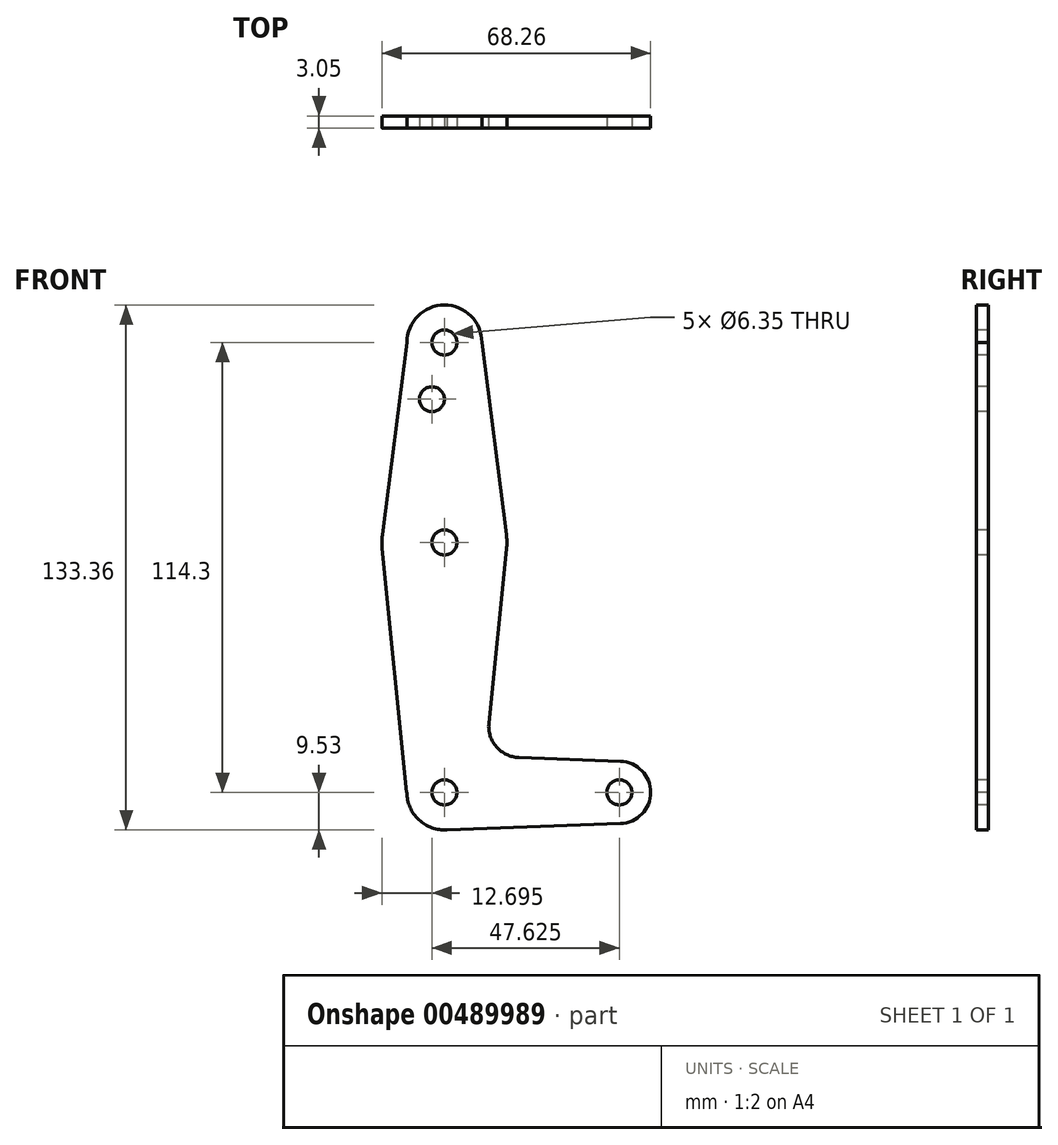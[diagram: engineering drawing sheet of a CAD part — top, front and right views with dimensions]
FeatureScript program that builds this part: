
annotation { "Feature Type Name" : "Feature", "Feature Type Description" : "" }
export const myFeature = defineFeature(function(context is Context, id is Id, definition is map)
    precondition{}
    {
        {
            var Q0;
            Q0=qCreatedBy(makeId("Front.planeOp"),FACE);
            var sketch = newSketch(context, id + "F0", { "sketchPlane" : qUnion([Q0])});
            skLineSegment(sketch, "E0", {"start": v(0, 114.3) * mm, "end": v(0, 0) * mm, "construction": true});
            skLineSegment(sketch, "E1", {"start": v(0, 0) * mm, "end": v(44.45, 0) * mm, "construction": true});
            skCircle(sketch, "E2", {"center": v(0, 114.3) * mm, "radius": 9.53 * mm});
            skCircle(sketch, "E3", {"center": v(0, 0) * mm, "radius": 9.53 * mm});
            skCircle(sketch, "E4", {"center": v(44.45, 0) * mm, "radius": 7.94 * mm});
            skCircle(sketch, "E5", {"center": v(0, 63.5) * mm, "radius": 15.88 * mm});
            skLineSegment(sketch, "E6", {"start": v(-9.57, 0) * mm, "end": v(9.53, 0) * mm});
            skLineSegment(sketch, "E7", {"start": v(0, 114.3) * mm, "end": v(9.52, 114.3) * mm});
            skLineSegment(sketch, "E8", {"start": v(9.53, 114.3) * mm, "end": v(15.75, 65.5) * mm});
            skLineSegment(sketch, "E9", {"start": v(-9.53, 114.3) * mm, "end": v(-15.75, 65.5) * mm});
            skLineSegment(sketch, "E10", {"start": v(-15.8, 61.91) * mm, "end": v(-9.57, 0) * mm});
            skLineSegment(sketch, "E11", {"start": v(15.8, 61.9) * mm, "end": v(11.3, 17.6) * mm});
            skLineSegment(sketch, "E12", {"start": v(18.93, 8.85) * mm, "end": v(44.73, 7.93) * mm});
            skLineSegment(sketch, "E13", {"start": v(0, -9.53) * mm, "end": v(44.73, -7.93) * mm});
            skCircle(sketch, "E14", {"center": v(0, 114.3) * mm, "radius": 3.18 * mm});
            skCircle(sketch, "E15", {"center": v(0, 63.5) * mm, "radius": 3.18 * mm});
            skCircle(sketch, "E16", {"center": v(0, 0) * mm, "radius": 3.18 * mm});
            skCircle(sketch, "E17", {"center": v(44.45, 0) * mm, "radius": 3.18 * mm});
            skCircle(sketch, "E18", {"center": v(-3.18, 99.89) * mm, "radius": 3.18 * mm});
            skPoint(sketch, "E19.newPointB", {"position": v(0, 9.53) * mm});
            skArc(sketch, "E19.filletArc", {"start": v(11.3, 17.6) * mm, "mid": v(13.22, 11.57) * mm, "end": v(18.93, 8.85) * mm});
            skSolve(sketch);
        }
        {
            var Q0;
            Q0 = qSketchRegion(id + "F0", true);
            extrude(context, id + "F1", {"entities" : qUnion([Q0]), "oppositeDirection" : true, "depth" : 3.05 * mm});
        }
    });
